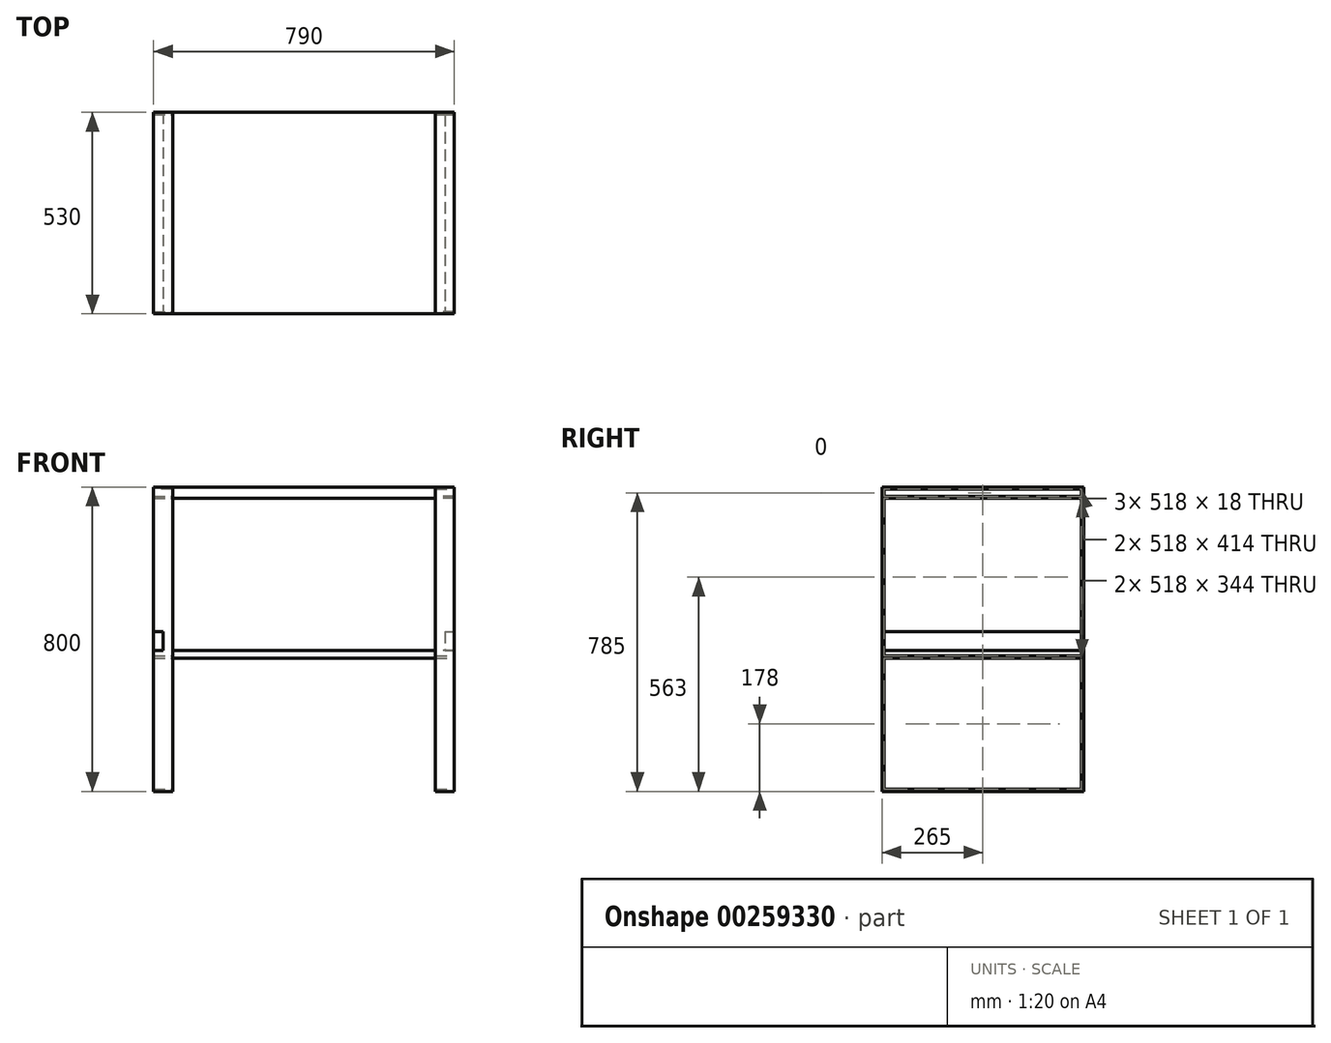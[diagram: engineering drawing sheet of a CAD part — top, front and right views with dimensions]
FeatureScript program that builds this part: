
annotation { "Feature Type Name" : "Feature", "Feature Type Description" : "" }
export const myFeature = defineFeature(function(context is Context, id is Id, definition is map)
    precondition{}
    {
        {
            assignVariable(context, id + "F0", {"name" : "largeur", "anyValue" : 790});
        }
        {
            assignVariable(context, id + "F1", {"name" : "hauteur", "anyValue" : 800});
        }
        {
            var Q0;
            Q0=qCreatedBy(makeId("Top.planeOp"),FACE);
            var sketch = newSketch(context, id + "F2", { "sketchPlane" : qUnion([Q0])});
            skLineSegment(sketch, "E0.bottom", {"start": v(-395, -259) * mm, "end": v(-345, -259) * mm});
            skLineSegment(sketch, "E0.top", {"start": v(-395, -265) * mm, "end": v(-345, -265) * mm});
            skLineSegment(sketch, "E0.left", {"start": v(-395, -259) * mm, "end": v(-395, -265) * mm});
            skLineSegment(sketch, "E0.right", {"start": v(-345, -259) * mm, "end": v(-345, -265) * mm});
            skLineSegment(sketch, "E1.MirrorCS", {"start": v(-345, 259) * mm, "end": v(-345, 265) * mm});
            skLineSegment(sketch, "E2.MirrorCS", {"start": v(-395, 259) * mm, "end": v(-395, 265) * mm});
            skLineSegment(sketch, "E3.MirrorCS", {"start": v(-395, 265) * mm, "end": v(-345, 265) * mm});
            skLineSegment(sketch, "E4.MirrorCS", {"start": v(-395, 259) * mm, "end": v(-345, 259) * mm});
            skLineSegment(sketch, "E5.MirrorCS", {"start": v(345, -259) * mm, "end": v(345, -265) * mm});
            skLineSegment(sketch, "E6.MirrorCS", {"start": v(395, 259) * mm, "end": v(395, 265) * mm});
            skLineSegment(sketch, "E7.MirrorCS", {"start": v(345, 259) * mm, "end": v(345, 265) * mm});
            skLineSegment(sketch, "E8.MirrorCS", {"start": v(395, -259) * mm, "end": v(395, -265) * mm});
            skLineSegment(sketch, "E9.MirrorCS", {"start": v(395, -259) * mm, "end": v(345, -259) * mm});
            skLineSegment(sketch, "E10.MirrorCS", {"start": v(395, -265) * mm, "end": v(345, -265) * mm});
            skLineSegment(sketch, "E11.MirrorCS", {"start": v(395, 265) * mm, "end": v(345, 265) * mm});
            skLineSegment(sketch, "E12.MirrorCS", {"start": v(395, 259) * mm, "end": v(345, 259) * mm});
            skSolve(sketch);
        }
        {
            var Q0;
            Q0 = qSketchRegion(id + "F2", true);
            extrude(context, id + "F3", {"entities" : qUnion([Q0]), "depth" : (getVariable(context, 'hauteur')) * mm});
        }
        {
            var Q0;
            Q0=makeQuery(id+"F3.opExtrude","SWEPT_FACE",FACE,{"disambiguationData":[OSD([sQuery(id+"F2.wireOp",EDGE,"E9.MirrorCS")])]});
            var sketch = newSketch(context, id + "F4", { "sketchPlane" : qUnion([Q0])});
            skLineSegment(sketch, "E13.bottom", {"start": v(-345, 800) * mm, "end": v(-395, 800) * mm});
            skLineSegment(sketch, "E13.top", {"start": v(-345, 794) * mm, "end": v(-395, 794) * mm});
            skLineSegment(sketch, "E13.left", {"start": v(-345, 800) * mm, "end": v(-345, 794) * mm});
            skLineSegment(sketch, "E13.right", {"start": v(-395, 800) * mm, "end": v(-395, 794) * mm});
            skLineSegment(sketch, "E14.bottom", {"start": v(-395, 776) * mm, "end": v(-345, 776) * mm});
            skLineSegment(sketch, "E14.top", {"start": v(-395, 770) * mm, "end": v(-345, 770) * mm});
            skLineSegment(sketch, "E14.left", {"start": v(-395, 776) * mm, "end": v(-395, 770) * mm});
            skLineSegment(sketch, "E14.right", {"start": v(-345, 776) * mm, "end": v(-345, 770) * mm});
            skLineSegment(sketch, "E15.MirrorCS", {"start": v(345, 776) * mm, "end": v(345, 770) * mm});
            skLineSegment(sketch, "E16.MirrorCS", {"start": v(395, 776) * mm, "end": v(345, 776) * mm});
            skLineSegment(sketch, "E17.MirrorCS", {"start": v(395, 776) * mm, "end": v(395, 770) * mm});
            skLineSegment(sketch, "E18.MirrorCS", {"start": v(395, 770) * mm, "end": v(345, 770) * mm});
            skLineSegment(sketch, "E19.MirrorCS", {"start": v(395, 800) * mm, "end": v(395, 794) * mm});
            skLineSegment(sketch, "E20.MirrorCS", {"start": v(345, 800) * mm, "end": v(395, 800) * mm});
            skLineSegment(sketch, "E21.MirrorCS", {"start": v(345, 794) * mm, "end": v(395, 794) * mm});
            skLineSegment(sketch, "E22.MirrorCS", {"start": v(345, 800) * mm, "end": v(345, 794) * mm});
            skLineSegment(sketch, "E23.bottom", {"start": v(-395, 0) * mm, "end": v(-345, 0) * mm});
            skLineSegment(sketch, "E23.top", {"start": v(-395, 6) * mm, "end": v(-345, 6) * mm});
            skLineSegment(sketch, "E23.left", {"start": v(-395, 0) * mm, "end": v(-395, 6) * mm});
            skLineSegment(sketch, "E23.right", {"start": v(-345, 0) * mm, "end": v(-345, 6) * mm});
            skLineSegment(sketch, "E24.MirrorCS", {"start": v(395, 0) * mm, "end": v(395, 6) * mm});
            skLineSegment(sketch, "E25.MirrorCS", {"start": v(395, 6) * mm, "end": v(345, 6) * mm});
            skLineSegment(sketch, "E26.MirrorCS", {"start": v(395, 0) * mm, "end": v(345, 0) * mm});
            skLineSegment(sketch, "E27.MirrorCS", {"start": v(345, 0) * mm, "end": v(345, 6) * mm});
            skLineSegment(sketch, "E28.bottom", {"start": v(-395, 356) * mm, "end": v(-345, 356) * mm});
            skLineSegment(sketch, "E28.top", {"start": v(-395, 350) * mm, "end": v(-345, 350) * mm});
            skLineSegment(sketch, "E28.left", {"start": v(-395, 356) * mm, "end": v(-395, 350) * mm});
            skLineSegment(sketch, "E28.right", {"start": v(-345, 356) * mm, "end": v(-345, 350) * mm});
            skLineSegment(sketch, "E29.MirrorCS", {"start": v(395, 356) * mm, "end": v(395, 350) * mm});
            skLineSegment(sketch, "E30.MirrorCS", {"start": v(395, 350) * mm, "end": v(345, 350) * mm});
            skLineSegment(sketch, "E31.MirrorCS", {"start": v(345, 356) * mm, "end": v(345, 350) * mm});
            skLineSegment(sketch, "E32.MirrorCS", {"start": v(395, 356) * mm, "end": v(345, 356) * mm});
            skSolve(sketch);
        }
        {
            var Q0;
            Q0 = qSketchRegion(id + "F4", true);
            extrude(context, id + "F5", {"entities" : qUnion([Q0]), "endBound" : BoundingType.UP_TO_NEXT, "depth" : 25 * mm});
        }
        {
            var Q0;
            Q0=makeQuery(id+"F3.opExtrude","SWEPT_BODY",BODY,{"disambiguationData":[OSD([sQuery(id+"F2.wireOp",EDGE,"E5.MirrorCS"),sQuery(id+"F2.wireOp",EDGE,"E8.MirrorCS"),sQuery(id+"F2.wireOp",EDGE,"E9.MirrorCS"),sQuery(id+"F2.wireOp",EDGE,"E10.MirrorCS")])]});
            var Q1;
            Q1=makeQuery(id+"F5.opExtrude","SWEPT_BODY",BODY,{"disambiguationData":[OSD([sQuery(id+"F4.wireOp",EDGE,"E13.bottom"),sQuery(id+"F4.wireOp",EDGE,"E13.top"),sQuery(id+"F4.wireOp",EDGE,"E13.left"),sQuery(id+"F4.wireOp",EDGE,"E13.right")])]});
            var Q2;
            Q2=makeQuery(id+"F5.opExtrude","SWEPT_BODY",BODY,{"disambiguationData":[OSD([sQuery(id+"F4.wireOp",EDGE,"E14.bottom"),sQuery(id+"F4.wireOp",EDGE,"E14.top"),sQuery(id+"F4.wireOp",EDGE,"E14.left"),sQuery(id+"F4.wireOp",EDGE,"E14.right")])]});
            var Q3;
            Q3=makeQuery(id+"F3.opExtrude","SWEPT_BODY",BODY,{"disambiguationData":[OSD([sQuery(id+"F2.wireOp",EDGE,"E6.MirrorCS"),sQuery(id+"F2.wireOp",EDGE,"E7.MirrorCS"),sQuery(id+"F2.wireOp",EDGE,"E11.MirrorCS"),sQuery(id+"F2.wireOp",EDGE,"E12.MirrorCS")])]});
            booleanBodies(context, id + "F6", {"operationType" : BooleanOperationType.UNION, "tools" : qUnion([Q0, Q1, Q2, Q3])});
        }
        {
            var Q0;
            Q0=makeQuery(id+"F3.opExtrude","SWEPT_BODY",BODY,{"disambiguationData":[OSD([sQuery(id+"F2.wireOp",EDGE,"E0.bottom"),sQuery(id+"F2.wireOp",EDGE,"E0.top"),sQuery(id+"F2.wireOp",EDGE,"E0.left"),sQuery(id+"F2.wireOp",EDGE,"E0.right")])]});
            var Q1;
            Q1=makeQuery(id+"F3.opExtrude","SWEPT_BODY",BODY,{"disambiguationData":[OSD([sQuery(id+"F2.wireOp",EDGE,"E1.MirrorCS"),sQuery(id+"F2.wireOp",EDGE,"E2.MirrorCS"),sQuery(id+"F2.wireOp",EDGE,"E3.MirrorCS"),sQuery(id+"F2.wireOp",EDGE,"E4.MirrorCS")])]});
            var Q2;
            Q2=makeQuery(id+"F5.opExtrude","SWEPT_BODY",BODY,{"disambiguationData":[OSD([sQuery(id+"F4.wireOp",EDGE,"E15.MirrorCS"),sQuery(id+"F4.wireOp",EDGE,"E16.MirrorCS"),sQuery(id+"F4.wireOp",EDGE,"E17.MirrorCS"),sQuery(id+"F4.wireOp",EDGE,"E18.MirrorCS")])]});
            var Q3;
            Q3=makeQuery(id+"F5.opExtrude","SWEPT_BODY",BODY,{"disambiguationData":[OSD([sQuery(id+"F4.wireOp",EDGE,"E19.MirrorCS"),sQuery(id+"F4.wireOp",EDGE,"E20.MirrorCS"),sQuery(id+"F4.wireOp",EDGE,"E21.MirrorCS"),sQuery(id+"F4.wireOp",EDGE,"E22.MirrorCS")])]});
            booleanBodies(context, id + "F7", {"operationType" : BooleanOperationType.UNION, "tools" : qUnion([Q0, Q1, Q2, Q3])});
        }
        {
            var Q0;
            Q0=makeQuery(id+"F5.opExtrude","SWEPT_BODY",BODY,{"disambiguationData":[OSD([sQuery(id+"F4.wireOp",EDGE,"E28.bottom"),sQuery(id+"F4.wireOp",EDGE,"E28.top"),sQuery(id+"F4.wireOp",EDGE,"E28.left"),sQuery(id+"F4.wireOp",EDGE,"E28.right")])]});
            var Q1;
            Q1=makeQuery(id+"F5.opExtrude","SWEPT_BODY",BODY,{"disambiguationData":[OSD([sQuery(id+"F4.wireOp",EDGE,"E23.bottom"),sQuery(id+"F4.wireOp",EDGE,"E23.top"),sQuery(id+"F4.wireOp",EDGE,"E23.left"),sQuery(id+"F4.wireOp",EDGE,"E23.right")])]});
            var Q2;
            Q2=makeQuery(id+"F3.opExtrude","SWEPT_BODY",BODY,{"disambiguationData":[OSD([sQuery(id+"F2.wireOp",EDGE,"E5.MirrorCS"),sQuery(id+"F2.wireOp",EDGE,"E8.MirrorCS"),sQuery(id+"F2.wireOp",EDGE,"E9.MirrorCS"),sQuery(id+"F2.wireOp",EDGE,"E10.MirrorCS")])]});
            booleanBodies(context, id + "F8", {"operationType" : BooleanOperationType.UNION, "tools" : qUnion([Q0, Q1, Q2])});
        }
        {
            var Q0;
            Q0=makeQuery(id+"F5.opExtrude","SWEPT_BODY",BODY,{"disambiguationData":[OSD([sQuery(id+"F4.wireOp",EDGE,"E29.MirrorCS"),sQuery(id+"F4.wireOp",EDGE,"E30.MirrorCS"),sQuery(id+"F4.wireOp",EDGE,"E31.MirrorCS"),sQuery(id+"F4.wireOp",EDGE,"E32.MirrorCS")])]});
            var Q1;
            Q1=makeQuery(id+"F5.opExtrude","SWEPT_BODY",BODY,{"disambiguationData":[OSD([sQuery(id+"F4.wireOp",EDGE,"E24.MirrorCS"),sQuery(id+"F4.wireOp",EDGE,"E25.MirrorCS"),sQuery(id+"F4.wireOp",EDGE,"E26.MirrorCS"),sQuery(id+"F4.wireOp",EDGE,"E27.MirrorCS")])]});
            var Q2;
            Q2=makeQuery(id+"F3.opExtrude","SWEPT_BODY",BODY,{"disambiguationData":[OSD([sQuery(id+"F2.wireOp",EDGE,"E0.bottom"),sQuery(id+"F2.wireOp",EDGE,"E0.top"),sQuery(id+"F2.wireOp",EDGE,"E0.left"),sQuery(id+"F2.wireOp",EDGE,"E0.right")])]});
            booleanBodies(context, id + "F9", {"operationType" : BooleanOperationType.UNION, "tools" : qUnion([Q0, Q1, Q2])});
        }
        {
            var Q0;
            Q0=qCreatedBy(makeId("Right.planeOp"),FACE);
            var sketch = newSketch(context, id + "F10", { "sketchPlane" : qUnion([Q0])});
            skLineSegment(sketch, "E33.bottom", {"start": v(265, 800) * mm, "end": v(-265, 800) * mm});
            skLineSegment(sketch, "E33.top", {"start": v(265, 770) * mm, "end": v(-265, 770) * mm});
            skLineSegment(sketch, "E33.left", {"start": v(265, 800) * mm, "end": v(265, 770) * mm});
            skLineSegment(sketch, "E33.right", {"start": v(-265, 800) * mm, "end": v(-265, 770) * mm});
            skLineSegment(sketch, "E34.bottom", {"start": v(265, 370) * mm, "end": v(-265, 370) * mm});
            skLineSegment(sketch, "E34.top", {"start": v(265, 350) * mm, "end": v(-265, 350) * mm});
            skLineSegment(sketch, "E34.left", {"start": v(265, 370) * mm, "end": v(265, 350) * mm});
            skLineSegment(sketch, "E34.right", {"start": v(-265, 370) * mm, "end": v(-265, 350) * mm});
            skSolve(sketch);
        }
        {
            var Q0;
            Q0 = qSketchRegion(id + "F10", true);
            extrude(context, id + "F11", {"entities" : qUnion([Q0]), "depth" : (getVariable(context, 'largeur') / 2) * mm, "hasSecondDirection" : true, "secondDirectionOppositeDirection" : true, "secondDirectionDepth" : (getVariable(context, 'largeur') / 2) * mm});
        }
        {
            var Q0;
            Q0=makeQuery(id+"F5.opExtrude","SWEPT_BODY",BODY,{"disambiguationData":[OSD([sQuery(id+"F4.wireOp",EDGE,"E29.MirrorCS"),sQuery(id+"F4.wireOp",EDGE,"E30.MirrorCS"),sQuery(id+"F4.wireOp",EDGE,"E31.MirrorCS"),sQuery(id+"F4.wireOp",EDGE,"E32.MirrorCS")])]});
            var Q1;
            Q1=makeQuery(id+"F5.opExtrude","SWEPT_BODY",BODY,{"disambiguationData":[OSD([sQuery(id+"F4.wireOp",EDGE,"E28.bottom"),sQuery(id+"F4.wireOp",EDGE,"E28.top"),sQuery(id+"F4.wireOp",EDGE,"E28.left"),sQuery(id+"F4.wireOp",EDGE,"E28.right")])]});
            var Q2;
            Q2=makeQuery(id+"F11.opExtrude","SWEPT_BODY",BODY,{"disambiguationData":[OSD([sQuery(id+"F10.wireOp",EDGE,"E34.bottom"),sQuery(id+"F10.wireOp",EDGE,"E34.top"),sQuery(id+"F10.wireOp",EDGE,"E34.left"),sQuery(id+"F10.wireOp",EDGE,"E34.right")])]});
            booleanBodies(context, id + "F12", {"operationType" : BooleanOperationType.SUBTRACTION, "tools" : qUnion([Q0, Q1]), "targets" : qUnion([Q2]), "keepTools" : true});
        }
        {
            var Q0;
            Q0=makeQuery(id+"F5.opExtrude","SWEPT_BODY",BODY,{"disambiguationData":[OSD([sQuery(id+"F4.wireOp",EDGE,"E29.MirrorCS"),sQuery(id+"F4.wireOp",EDGE,"E30.MirrorCS"),sQuery(id+"F4.wireOp",EDGE,"E31.MirrorCS"),sQuery(id+"F4.wireOp",EDGE,"E32.MirrorCS")])]});
            var Q1;
            Q1=makeQuery(id+"F5.opExtrude","SWEPT_BODY",BODY,{"disambiguationData":[OSD([sQuery(id+"F4.wireOp",EDGE,"E28.bottom"),sQuery(id+"F4.wireOp",EDGE,"E28.top"),sQuery(id+"F4.wireOp",EDGE,"E28.left"),sQuery(id+"F4.wireOp",EDGE,"E28.right")])]});
            var Q2;
            Q2=makeQuery(id+"F11.opExtrude","SWEPT_BODY",BODY,{"disambiguationData":[OSD([sQuery(id+"F10.wireOp",EDGE,"E33.bottom"),sQuery(id+"F10.wireOp",EDGE,"E33.top"),sQuery(id+"F10.wireOp",EDGE,"E33.left"),sQuery(id+"F10.wireOp",EDGE,"E33.right")])]});
            booleanBodies(context, id + "F13", {"operationType" : BooleanOperationType.SUBTRACTION, "tools" : qUnion([Q0, Q1]), "targets" : qUnion([Q2]), "keepTools" : true});
        }
        {
            var Q0;
            Q0=makeQuery(id+"F11.opExtrude","SWEPT_FACE",FACE,{"disambiguationData":[OSD([sQuery(id+"F10.wireOp",EDGE,"E34.bottom")])]});
            var sketch = newSketch(context, id + "F14", { "sketchPlane" : qUnion([Q0])});
            skPoint(sketch, "E35.oppositeSnap0", {"position": v(370, -259) * mm});
            skLineSegment(sketch, "E35.bottom", {"start": v(395, 265) * mm, "end": v(370, 265) * mm});
            skLineSegment(sketch, "E35.top", {"start": v(395, -265) * mm, "end": v(370, -265) * mm});
            skLineSegment(sketch, "E35.left", {"start": v(395, 265) * mm, "end": v(395, -265) * mm});
            skLineSegment(sketch, "E35.right", {"start": v(370, 265) * mm, "end": v(370, -265) * mm});
            skPoint(sketch, "E36.MirrorP", {"position": v(-370, -259) * mm});
            skLineSegment(sketch, "E37.MirrorCS", {"start": v(-395, 265) * mm, "end": v(-395, -265) * mm});
            skLineSegment(sketch, "E38.MirrorCS", {"start": v(-370, 265) * mm, "end": v(-370, -265) * mm});
            skLineSegment(sketch, "E39.MirrorCS", {"start": v(-395, 265) * mm, "end": v(-370, 265) * mm});
            skLineSegment(sketch, "E40.MirrorCS", {"start": v(-395, -265) * mm, "end": v(-370, -265) * mm});
            skSolve(sketch);
        }
        {
            var Q0;
            Q0 = qSketchRegion(id + "F14", true);
            extrude(context, id + "F15", {"entities" : qUnion([Q0]), "depth" : 50 * mm, "offsetDistance" : 25 * mm});
        }
        {
            var Q0;
            Q0=makeQuery(id+"F5.opExtrude","SWEPT_BODY",BODY,{"disambiguationData":[OSD([sQuery(id+"F4.wireOp",EDGE,"E28.bottom"),sQuery(id+"F4.wireOp",EDGE,"E28.top"),sQuery(id+"F4.wireOp",EDGE,"E28.left"),sQuery(id+"F4.wireOp",EDGE,"E28.right")])]});
            var Q1;
            Q1=makeQuery(id+"F5.opExtrude","SWEPT_BODY",BODY,{"disambiguationData":[OSD([sQuery(id+"F4.wireOp",EDGE,"E29.MirrorCS"),sQuery(id+"F4.wireOp",EDGE,"E30.MirrorCS"),sQuery(id+"F4.wireOp",EDGE,"E31.MirrorCS"),sQuery(id+"F4.wireOp",EDGE,"E32.MirrorCS")])]});
            var Q2;
            Q2=makeQuery(id+"F15.opExtrude","SWEPT_BODY",BODY,{"disambiguationData":[OSD([sQuery(id+"F14.wireOp",EDGE,"E35.bottom"),sQuery(id+"F14.wireOp",EDGE,"E35.top"),sQuery(id+"F14.wireOp",EDGE,"E35.left"),sQuery(id+"F14.wireOp",EDGE,"E35.right")])]});
            booleanBodies(context, id + "F16", {"operationType" : BooleanOperationType.SUBTRACTION, "tools" : qUnion([Q0, Q1]), "targets" : qUnion([Q2]), "keepTools" : true});
        }
    });
